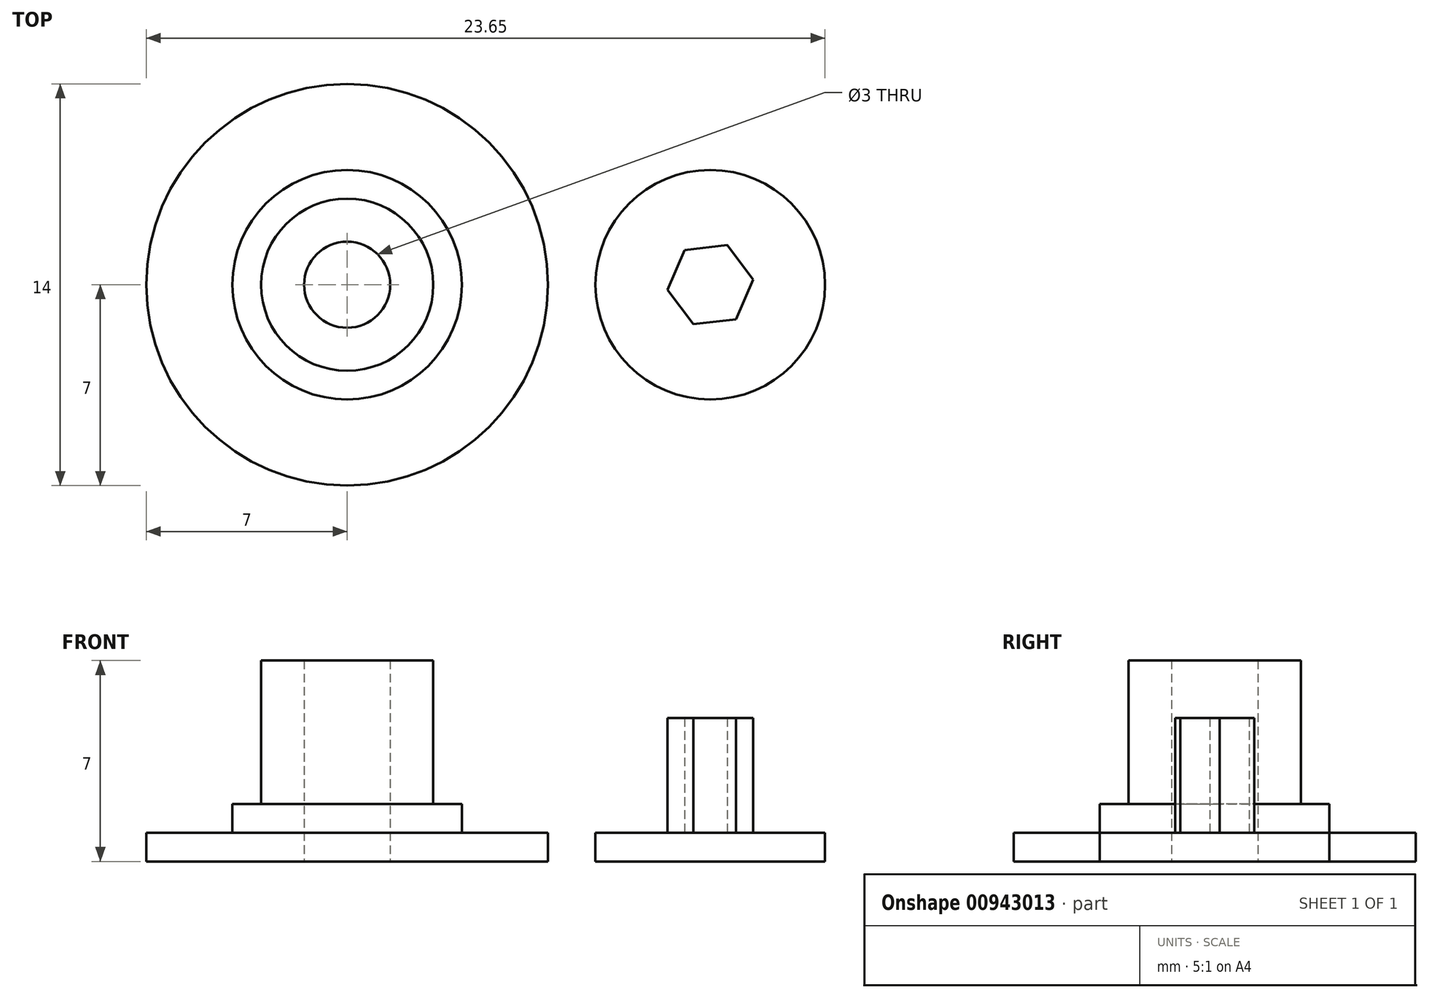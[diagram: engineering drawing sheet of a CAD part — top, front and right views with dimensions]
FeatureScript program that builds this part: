
annotation { "Feature Type Name" : "Feature", "Feature Type Description" : "" }
export const myFeature = defineFeature(function(context is Context, id is Id, definition is map)
    precondition{}
    {
        {
            var Q0;
            Q0=qCreatedBy(makeId("Top.planeOp"),FACE);
            var sketch = newSketch(context, id + "F0", { "sketchPlane" : qUnion([Q0])});
            skCircle(sketch, "E0", {"center": v(0, 0) * mm, "radius": 7 * mm});
            skCircle(sketch, "E1", {"center": v(0, 0) * mm, "radius": 3 * mm});
            skCircle(sketch, "E2", {"center": v(0, 0) * mm, "radius": 4 * mm});
            skCircle(sketch, "E3", {"center": v(0, 0) * mm, "radius": 1.5 * mm});
            skSolve(sketch);
        }
        {
            var Q0;
            Q0 = qSketchRegion(id + "F0", true);
            var Q1;
            Q1=makeQuery(id+"F0.imprint","IMPRINT",FACE,{"disambiguationData":[TD([[makeQuery(id+"F0.imprint","IMPRINT",EDGE,{"derivedFrom":sQuery(id+"F0.wireOp",EDGE,"E0")}),1.0]])]});
            extrude(context, id + "F1", {"entities" : qUnion([Q0, Q1]), "depth" : 1 * mm, "offsetDistance" : 25 * mm});
        }
        {
            var Q0;
            Q0=makeQuery(id+"F0.imprint","IMPRINT",FACE,{"disambiguationData":[TD([[makeQuery(id+"F0.imprint","IMPRINT",EDGE,{"derivedFrom":sQuery(id+"F0.wireOp",EDGE,"E1")}),-1.0]])]});
            extrude(context, id + "F2", {"entities" : qUnion([Q0]), "operationType" : NewBodyOperationType.ADD, "depth" : 2 * mm, "offsetDistance" : 25 * mm});
        }
        {
            var Q0;
            Q0=makeQuery(id+"F0.imprint","IMPRINT",FACE,{"disambiguationData":[TD([[makeQuery(id+"F0.imprint","IMPRINT",EDGE,{"derivedFrom":sQuery(id+"F0.wireOp",EDGE,"E1")}),1.0]])]});
            extrude(context, id + "F3", {"entities" : qUnion([Q0]), "operationType" : NewBodyOperationType.ADD, "depth" : 7 * mm, "offsetDistance" : 25 * mm});
        }
        {
            var Q0;
            Q0=qCreatedBy(makeId("Top.planeOp"),FACE);
            var sketch = newSketch(context, id + "F4", { "sketchPlane" : qUnion([Q0])});
            skCircle(sketch, "E4.cCircle", {"center": v(12.65, 0) * mm, "radius": 1.5 * mm, "construction": true});
            skLineSegment(sketch, "E4.0", {"start": v(13.55, -1.2) * mm, "end": v(12.06, -1.38) * mm});
            skLineSegment(sketch, "E4.1", {"start": v(12.06, -1.38) * mm, "end": v(11.16, -0.18) * mm});
            skLineSegment(sketch, "E4.2", {"start": v(11.16, -0.18) * mm, "end": v(11.76, 1.2) * mm});
            skLineSegment(sketch, "E4.3", {"start": v(11.76, 1.2) * mm, "end": v(13.24, 1.38) * mm});
            skLineSegment(sketch, "E4.4", {"start": v(13.24, 1.38) * mm, "end": v(14.14, 0.18) * mm});
            skLineSegment(sketch, "E4.5", {"start": v(14.14, 0.18) * mm, "end": v(13.55, -1.2) * mm});
            skCircle(sketch, "E5", {"center": v(12.65, 0) * mm, "radius": 4 * mm});
            skSolve(sketch);
        }
        {
            var Q0;
            Q0 = qSketchRegion(id + "F4", true);
            extrude(context, id + "F5", {"entities" : qUnion([Q0]), "depth" : 1 * mm, "offsetDistance" : 25 * mm});
        }
        {
            var Q0;
            Q0=makeQuery(id+"F4.imprint","IMPRINT",FACE,{"disambiguationData":[TD([[makeQuery(id+"F4.imprint","IMPRINT",EDGE,{"derivedFrom":sQuery(id+"F4.wireOp",EDGE,"E4.0")}),-1.0]])]});
            extrude(context, id + "F6", {"entities" : qUnion([Q0]), "operationType" : NewBodyOperationType.ADD, "depth" : 5 * mm, "offsetDistance" : 25 * mm});
        }
    });
